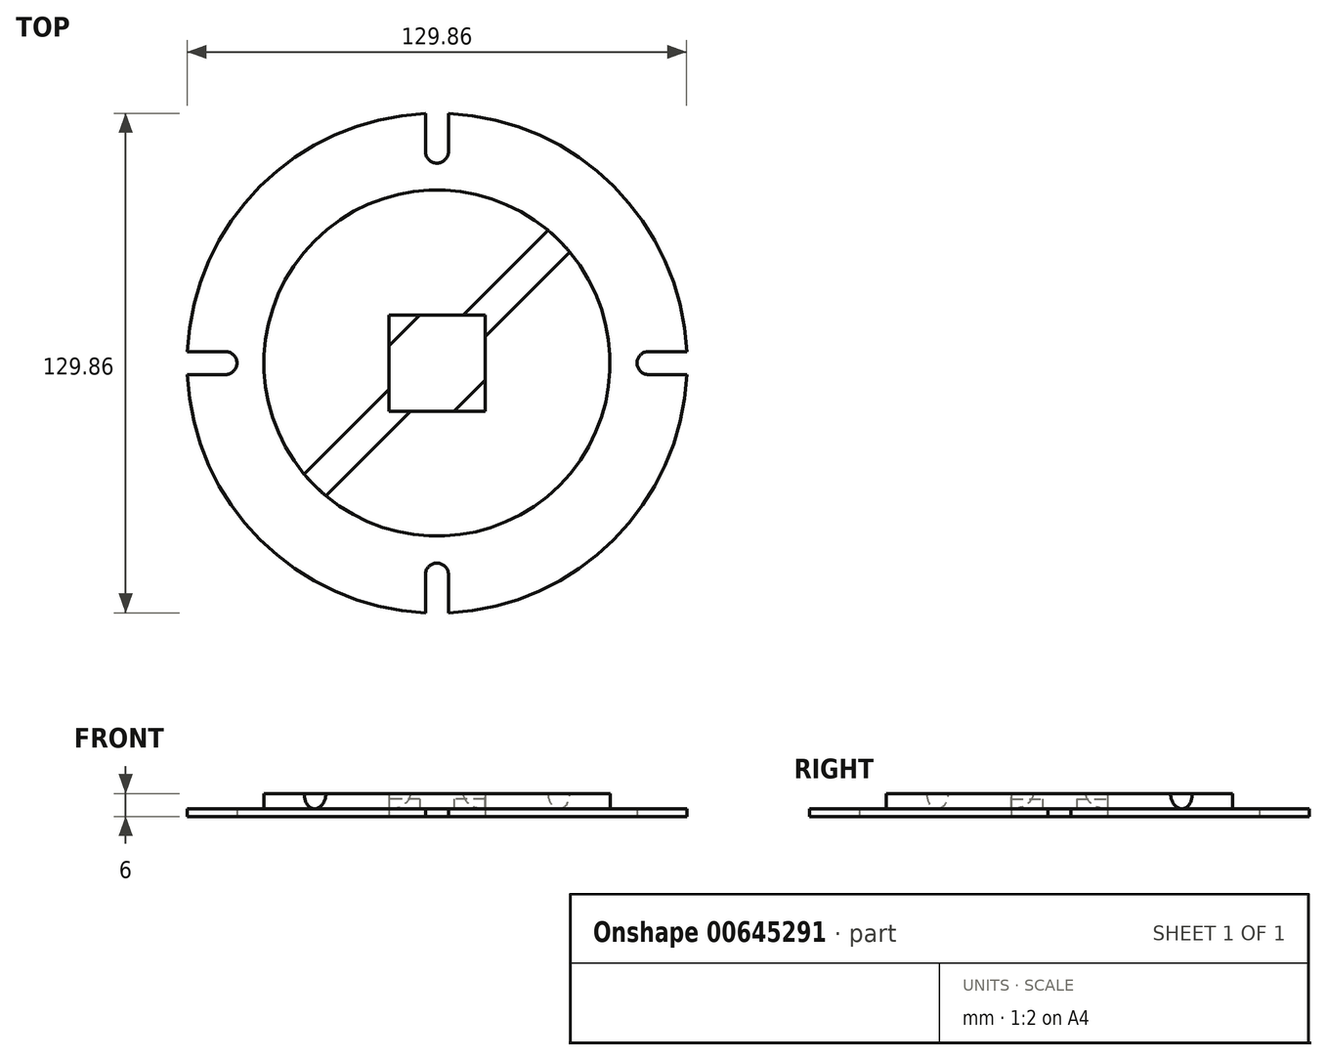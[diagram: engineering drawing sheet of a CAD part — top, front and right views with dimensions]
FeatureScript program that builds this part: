
annotation { "Feature Type Name" : "Feature", "Feature Type Description" : "" }
export const myFeature = defineFeature(function(context is Context, id is Id, definition is map)
    precondition{}
    {
        {
            var Q0;
            Q0=qCreatedBy(makeId("Top.planeOp"),FACE);
            var sketch = newSketch(context, id + "F0", { "sketchPlane" : qUnion([Q0])});
            skCircle(sketch, "E0", {"center": v(0, 0) * mm, "radius": 65 * mm});
            skCircle(sketch, "E1", {"center": v(0, 0) * mm, "radius": 45 * mm});
            skLineSegment(sketch, "E2", {"start": v(0, -45) * mm, "end": v(0, -65) * mm});
            skPoint(sketch, "E3", {"position": v(0, -55) * mm});
            skArc(sketch, "E4", {"start": v(-3, -55) * mm, "mid": v(0, -52) * mm, "end": v(3, -55) * mm});
            skLineSegment(sketch, "E5", {"start": v(-3, -55) * mm, "end": v(-3, -64.93) * mm});
            skLineSegment(sketch, "E6", {"start": v(3, -55) * mm, "end": v(3, -64.93) * mm});
            skArc(sketch, "E7.1.0", {"start": v(55, -3) * mm, "mid": v(52, 0) * mm, "end": v(55, 3) * mm});
            skLineSegment(sketch, "E7.1.1", {"start": v(55, -3) * mm, "end": v(64.93, -3) * mm});
            skLineSegment(sketch, "E7.1.2", {"start": v(55, 3) * mm, "end": v(64.93, 3) * mm});
            skArc(sketch, "E7.2.0", {"start": v(3, 55) * mm, "mid": v(0, 52) * mm, "end": v(-3, 55) * mm});
            skLineSegment(sketch, "E7.2.1", {"start": v(3, 55) * mm, "end": v(3, 64.93) * mm});
            skLineSegment(sketch, "E7.2.2", {"start": v(-3, 55) * mm, "end": v(-3, 64.93) * mm});
            skArc(sketch, "E7.3.0", {"start": v(-55, 3) * mm, "mid": v(-52, 0) * mm, "end": v(-55, -3) * mm});
            skLineSegment(sketch, "E7.3.1", {"start": v(-55, 3) * mm, "end": v(-64.93, 3) * mm});
            skLineSegment(sketch, "E7.3.2", {"start": v(-55, -3) * mm, "end": v(-64.93, -3) * mm});
            skSolve(sketch);
        }
        {
            var Q0;
            Q0=qCreatedBy(makeId("Top.planeOp"),FACE);
            var sketch = newSketch(context, id + "F1", { "sketchPlane" : qUnion([Q0])});
            skLineSegment(sketch, "E8.bottom", {"start": v(12.5, -12.5) * mm, "end": v(-12.5, -12.5) * mm});
            skLineSegment(sketch, "E8.top", {"start": v(12.5, 12.5) * mm, "end": v(-12.5, 12.5) * mm});
            skLineSegment(sketch, "E8.left", {"start": v(12.5, -12.5) * mm, "end": v(12.5, 12.5) * mm});
            skLineSegment(sketch, "E8.right", {"start": v(-12.5, -12.5) * mm, "end": v(-12.5, 12.5) * mm});
            skPoint(sketch, "E8.middle", {"position": v(0, 0) * mm});
            skCircle(sketch, "E9", {"center": v(0, 0) * mm, "radius": 10.5 * mm});
            skLineSegment(sketch, "E10", {"start": v(-12.5, -12.5) * mm, "end": v(12.5, 12.5) * mm});
            skLineSegment(sketch, "E11", {"start": v(4.47, -12.5) * mm, "end": v(12.5, -4.47) * mm});
            skLineSegment(sketch, "E12.MirrorCS", {"start": v(-12.5, 4.47) * mm, "end": v(-4.47, 12.5) * mm});
            skSolve(sketch);
        }
        {
            var Q0;
            Q0=makeQuery(id+"F0.imprint","IMPRINT",FACE,{"disambiguationData":[TD([[makeQuery(id+"F0.imprint","IMPRINT",EDGE,{"derivedFrom":sQuery(id+"F0.wireOp",EDGE,"E0")}),1.0]])]});
            extrude(context, id + "F2", {"entities" : qUnion([Q0]), "depth" : 2 * mm, "offsetDistance" : 25 * mm});
        }
        {
            var Q0;
            Q0=makeQuery(id+"F0.imprint","IMPRINT",FACE,{"disambiguationData":[TD([[makeQuery(id+"F0.imprint","IMPRINT",EDGE,{"derivedFrom":sQuery(id+"F0.wireOp",EDGE,"E1")}),1.0]])]});
            extrude(context, id + "F3", {"entities" : qUnion([Q0]), "operationType" : NewBodyOperationType.ADD, "depth" : 6 * mm, "offsetDistance" : 25 * mm});
        }
        {
            var Q0;
            {var subQ3=sQuery(id+"F1.wireOp",EDGE,"E11");Q0=makeQuery(id+"F1.imprint","IMPRINT",FACE,{"disambiguationData":[TD([[makeQuery(id+"F1.imprint","IMPRINT",EDGE,{"derivedFrom":subQ3}),-1.0]])]});}
            var Q1;
            {var subQ8=sQuery(id+"F1.wireOp",EDGE,"E11");Q1=makeQuery(id+"F1.imprint","IMPRINT",FACE,{"disambiguationData":[TD([[makeQuery(id+"F1.imprint","IMPRINT",EDGE,{"derivedFrom":subQ8}),1.0]])]});}
            var Q2;
            {var subQ6=sQuery(id+"F1.wireOp",EDGE,"E12.MirrorCS");Q2=makeQuery(id+"F1.imprint","IMPRINT",FACE,{"disambiguationData":[TD([[makeQuery(id+"F1.imprint","IMPRINT",EDGE,{"derivedFrom":subQ6}),-1.0]])]});}
            var Q3;
            {var subQ3=sQuery(id+"F1.wireOp",EDGE,"E12.MirrorCS");Q3=makeQuery(id+"F1.imprint","IMPRINT",FACE,{"disambiguationData":[TD([[makeQuery(id+"F1.imprint","IMPRINT",EDGE,{"derivedFrom":subQ3}),1.0]])]});}
            var Q4;
            {var subQ0=sQuery(id+"F1.wireOp",EDGE,"E10");var subQ1=sQuery(id+"F1.wireOp",EDGE,"E9");var subQ2=makeQuery(id+"F1.imprint","INTERSECT",VERTEX,{"disambiguationData":[OD(0.0)],"derivedFrom":[subQ1,subQ0]});Q4=makeQuery(id+"F1.imprint","IMPRINT",FACE,{"disambiguationData":[TD([[makeQuery(id+"F1.imprint","IMPRINT",EDGE,{"disambiguationData":[TD([[subQ2,1.0]])],"derivedFrom":subQ1}),1.0]])]});}
            var Q5;
            {var subQ0=sQuery(id+"F1.wireOp",EDGE,"E10");var subQ1=sQuery(id+"F1.wireOp",EDGE,"E9");var subQ2=makeQuery(id+"F1.imprint","INTERSECT",VERTEX,{"disambiguationData":[OD(0.0)],"derivedFrom":[subQ1,subQ0]});Q5=makeQuery(id+"F1.imprint","IMPRINT",FACE,{"disambiguationData":[TD([[makeQuery(id+"F1.imprint","IMPRINT",EDGE,{"disambiguationData":[TD([[subQ2,-1.0]])],"derivedFrom":subQ1}),1.0]])]});}
            extrude(context, id + "F4", {"entities" : qUnion([Q0, Q1, Q2, Q3, Q4, Q5]), "operationType" : NewBodyOperationType.REMOVE, "depth" : 6 * mm, "offsetDistance" : 25 * mm});
        }
        {
            var Q0;
            {var subQ3=sQuery(id+"F1.wireOp",EDGE,"E12.MirrorCS");Q0=makeQuery(id+"F1.imprint","IMPRINT",FACE,{"disambiguationData":[TD([[makeQuery(id+"F1.imprint","IMPRINT",EDGE,{"derivedFrom":subQ3}),1.0]])]});}
            var Q1;
            {var subQ3=sQuery(id+"F1.wireOp",EDGE,"E11");Q1=makeQuery(id+"F1.imprint","IMPRINT",FACE,{"disambiguationData":[TD([[makeQuery(id+"F1.imprint","IMPRINT",EDGE,{"derivedFrom":subQ3}),-1.0]])]});}
            extrude(context, id + "F5", {"entities" : qUnion([Q0, Q1]), "operationType" : NewBodyOperationType.ADD, "depth" : 4.6 * mm, "offsetDistance" : 25 * mm});
        }
        {
            var Q0;
            Q0=qCreatedBy(makeId("Front.planeOp"),FACE);
            var sketch = newSketch(context, id + "F6", { "sketchPlane" : qUnion([Q0])});
            skLineSegment(sketch, "E13", {"start": v(0, 0) * mm, "end": v(0, 68.6) * mm});
            skSolve(sketch);
        }
        {
            var Q0;
            Q0=sQuery(id+"F6.wireOp",EDGE,"E13");
            var Q1;
            Q1=qCreatedBy(makeId("Front.planeOp"),FACE);
            cPlane(context, id + "F7", {"entities" : qUnion([Q0, Q1]), "cplaneType" : CPlaneType.LINE_ANGLE, "offset" : 25 * mm, "angle" : 45 * degree, "oppositeDirection" : true, "width" : 150 * mm, "height" : 150 * mm});
        }
        {
            var Q0;
            Q0=qCreatedBy(id+"F7.planeOp",FACE);
            var sketch = newSketch(context, id + "F8", { "sketchPlane" : qUnion([Q0])});
            skLineSegment(sketch, "E14", {"start": v(0, 0) * mm, "end": v(0, 2) * mm});
            skLineSegment(sketch, "E15", {"start": v(0, 2) * mm, "end": v(0, 2) * mm});
            skLineSegment(sketch, "E16", {"start": v(0, 2) * mm, "end": v(0, 6) * mm});
            skCircle(sketch, "E17", {"center": v(0, 6) * mm, "radius": 4 * mm});
            skSolve(sketch);
        }
        {
            var Q0;
            Q0=makeQuery(id+"F8.imprint","IMPRINT",FACE,{"disambiguationData":[TD([[makeQuery(id+"F8.imprint","IMPRINT",EDGE,{"derivedFrom":sQuery(id+"F8.wireOp",EDGE,"E17")}),1.0]])]});
            extrude(context, id + "F9", {"entities" : qUnion([Q0]), "operationType" : NewBodyOperationType.REMOVE, "oppositeDirection" : true, "depth" : 45 * mm, "offsetDistance" : 25 * mm, "hasSecondDirection" : true, "secondDirectionOppositeDirection" : false, "secondDirectionDepth" : 45 * mm});
        }
    });
